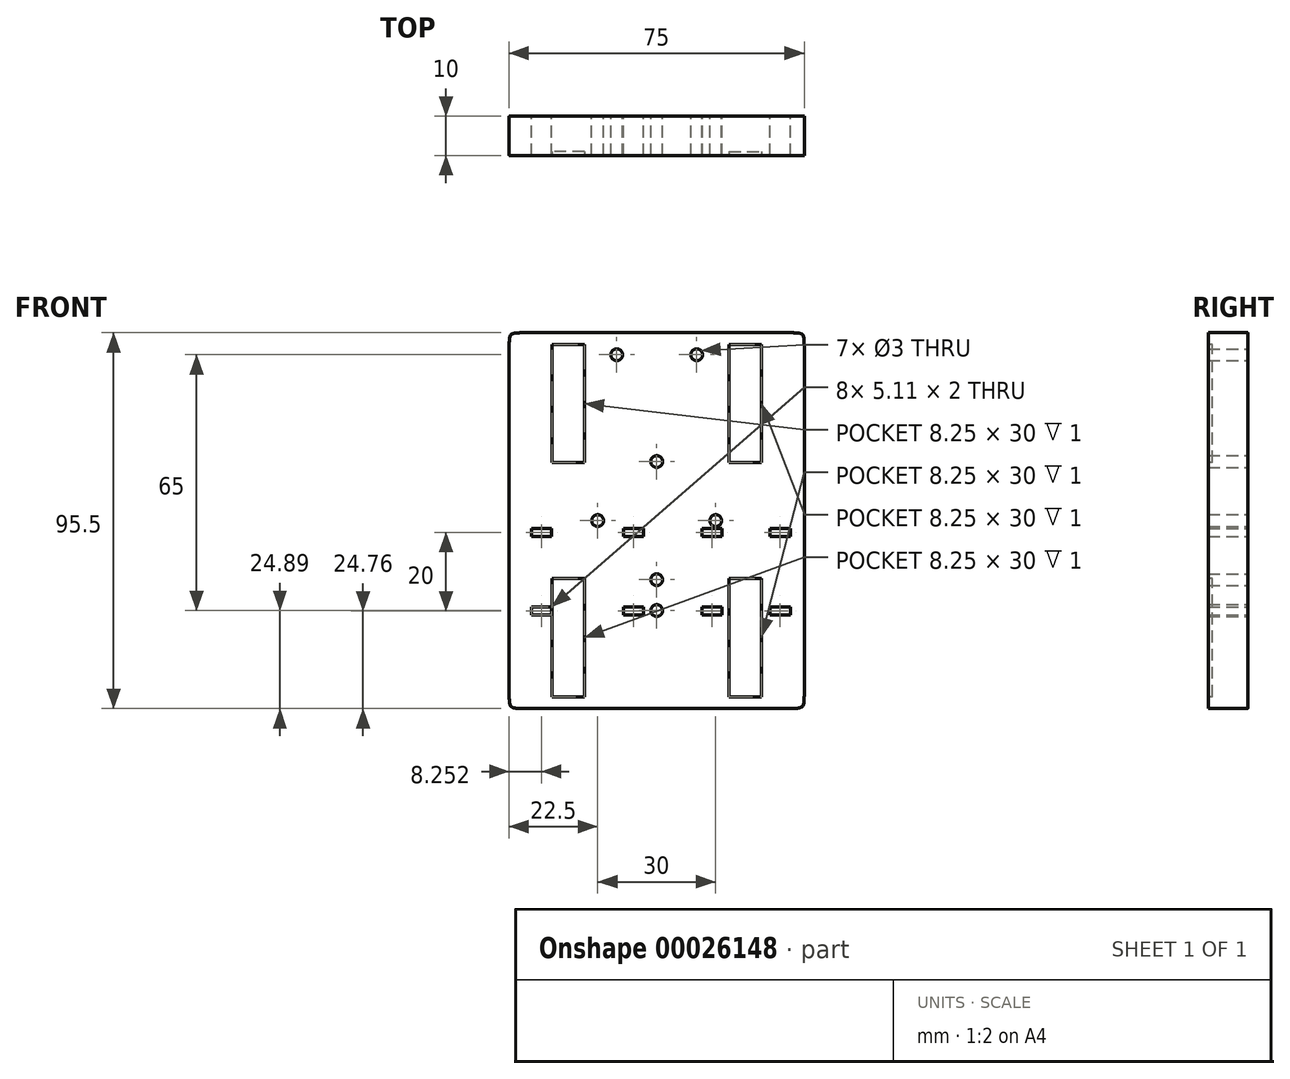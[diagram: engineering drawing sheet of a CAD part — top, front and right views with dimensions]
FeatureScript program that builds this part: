
annotation { "Feature Type Name" : "Feature", "Feature Type Description" : "" }
export const myFeature = defineFeature(function(context is Context, id is Id, definition is map)
    precondition{}
    {
        {
            var Q0;
            Q0=qCreatedBy(makeId("Front.planeOp"),FACE);
            var sketch = newSketch(context, id + "F0", { "sketchPlane" : qUnion([Q0])});
            skLineSegment(sketch, "E0.rect.bottom", {"start": v(37.5, -47.75) * mm, "end": v(-37.5, -47.75) * mm});
            skLineSegment(sketch, "E0.rect.top", {"start": v(37.5, 47.75) * mm, "end": v(-37.5, 47.75) * mm});
            skLineSegment(sketch, "E0.rect.left", {"start": v(37.5, -47.75) * mm, "end": v(37.5, 47.75) * mm});
            skLineSegment(sketch, "E0.rect.right", {"start": v(-37.5, -47.75) * mm, "end": v(-37.5, 47.75) * mm});
            skPoint(sketch, "E0.rect.middle", {"position": v(0, 0) * mm});
            skLineSegment(sketch, "E1.trimOffspring", {"start": v(-10.16, -22.86) * mm, "end": v(10.16, -22.86) * mm, "construction": true});
            skPoint(sketch, "E2", {"position": v(0, -22.86) * mm});
            skLineSegment(sketch, "E3", {"start": v(0, 47.75) * mm, "end": v(0, -47.75) * mm, "construction": true});
            skLineSegment(sketch, "E4", {"start": v(-22.5, 47.75) * mm, "end": v(-22.5, -47.75) * mm, "construction": true});
            skLineSegment(sketch, "E5", {"start": v(22.5, 47.75) * mm, "end": v(22.5, -47.75) * mm, "construction": true});
            skLineSegment(sketch, "E6", {"start": v(-22.5, 47.75) * mm, "end": v(22.5, -47.75) * mm, "construction": true});
            skLineSegment(sketch, "E7.rect.bottom", {"start": v(-18.37, 14.75) * mm, "end": v(-26.62, 14.75) * mm});
            skLineSegment(sketch, "E7.rect.top", {"start": v(-18.38, 44.75) * mm, "end": v(-26.63, 44.75) * mm});
            skLineSegment(sketch, "E7.rect.left", {"start": v(-18.37, 14.75) * mm, "end": v(-18.38, 44.75) * mm});
            skLineSegment(sketch, "E7.rect.right", {"start": v(-26.62, 14.75) * mm, "end": v(-26.63, 44.75) * mm});
            skPoint(sketch, "E7.rect.middle", {"position": v(-22.5, 29.75) * mm});
            skLineSegment(sketch, "E8.rect.bottom", {"start": v(-18.37, -44.75) * mm, "end": v(-26.62, -44.75) * mm});
            skLineSegment(sketch, "E8.rect.top", {"start": v(-18.37, -14.75) * mm, "end": v(-26.62, -14.75) * mm});
            skLineSegment(sketch, "E8.rect.left", {"start": v(-18.37, -44.75) * mm, "end": v(-18.37, -14.75) * mm});
            skLineSegment(sketch, "E8.rect.right", {"start": v(-26.62, -44.75) * mm, "end": v(-26.62, -14.75) * mm});
            skPoint(sketch, "E8.rect.middle", {"position": v(-22.5, -29.75) * mm});
            skLineSegment(sketch, "E9.rect.bottom", {"start": v(26.63, 14.75) * mm, "end": v(18.38, 14.75) * mm});
            skLineSegment(sketch, "E9.rect.top", {"start": v(26.62, 44.75) * mm, "end": v(18.37, 44.75) * mm});
            skLineSegment(sketch, "E9.rect.left", {"start": v(26.63, 14.75) * mm, "end": v(26.62, 44.75) * mm});
            skLineSegment(sketch, "E9.rect.right", {"start": v(18.38, 14.75) * mm, "end": v(18.37, 44.75) * mm});
            skPoint(sketch, "E9.rect.middle", {"position": v(22.5, 29.75) * mm});
            skLineSegment(sketch, "E10.rect.bottom", {"start": v(26.62, -14.75) * mm, "end": v(18.37, -14.75) * mm});
            skLineSegment(sketch, "E10.rect.top", {"start": v(26.62, -44.75) * mm, "end": v(18.38, -44.75) * mm});
            skLineSegment(sketch, "E10.rect.left", {"start": v(26.62, -14.75) * mm, "end": v(26.62, -44.75) * mm});
            skLineSegment(sketch, "E10.rect.right", {"start": v(18.37, -14.75) * mm, "end": v(18.38, -44.75) * mm});
            skPoint(sketch, "E10.rect.middle", {"position": v(22.5, -29.75) * mm});
            skLineSegment(sketch, "E11", {"start": v(-37.5, 44.75) * mm, "end": v(37.5, 44.75) * mm, "construction": true});
            skLineSegment(sketch, "E12", {"start": v(-37.5, -44.75) * mm, "end": v(37.5, -44.75) * mm, "construction": true});
            skPoint(sketch, "E13.orphan", {"position": v(37.5, 34.75) * mm});
            skPoint(sketch, "E14.orphan", {"position": v(0, 34.75) * mm});
            skPoint(sketch, "E15.start.orphan", {"position": v(-37.5, 34.75) * mm});
            skLineSegment(sketch, "E16", {"start": v(0, 0) * mm, "end": v(32.27, 0) * mm, "construction": true});
            skCircle(sketch, "E17.MirrorC", {"center": v(10.16, 42.14) * mm, "radius": 1.5 * mm});
            skCircle(sketch, "E18.MirrorC", {"center": v(-10.16, 42.14) * mm, "radius": 1.5 * mm});
            skCircle(sketch, "E19", {"center": v(0, 15) * mm, "radius": 1.5 * mm});
            skCircle(sketch, "E20.1.1", {"center": v(-15, 0) * mm, "radius": 1.5 * mm});
            skCircle(sketch, "E20.2.1", {"center": v(0, -15) * mm, "radius": 1.5 * mm});
            skCircle(sketch, "E20.3.1", {"center": v(15, 0) * mm, "radius": 1.5 * mm});
            skLineSegment(sketch, "E21", {"start": v(10.16, 42.14) * mm, "end": v(-10.16, 42.14) * mm, "construction": true});
            skLineSegment(sketch, "E22", {"start": v(-37.5, -2.99) * mm, "end": v(37.5, -2.99) * mm, "construction": true});
            skCircle(sketch, "E23", {"center": v(0, -22.86) * mm, "radius": 1.5 * mm});
            skLineSegment(sketch, "E24", {"start": v(-37.5, -22.99) * mm, "end": v(37.5, -22.99) * mm, "construction": true});
            skLineSegment(sketch, "E25.rect.bottom", {"start": v(-26.7, -3.99) * mm, "end": v(-31.8, -3.99) * mm});
            skLineSegment(sketch, "E25.rect.top", {"start": v(-26.7, -1.99) * mm, "end": v(-31.8, -1.99) * mm});
            skLineSegment(sketch, "E25.rect.left", {"start": v(-26.7, -3.99) * mm, "end": v(-26.7, -1.99) * mm});
            skLineSegment(sketch, "E25.rect.right", {"start": v(-31.8, -3.99) * mm, "end": v(-31.8, -1.99) * mm});
            skPoint(sketch, "E25.rect.middle", {"position": v(-29.25, -2.99) * mm});
            skLineSegment(sketch, "E26.rect.bottom", {"start": v(-8.4, -1.99) * mm, "end": v(-3.3, -1.99) * mm});
            skLineSegment(sketch, "E26.rect.top", {"start": v(-8.4, -4) * mm, "end": v(-3.3, -4) * mm});
            skLineSegment(sketch, "E26.rect.left", {"start": v(-8.4, -1.99) * mm, "end": v(-8.4, -4) * mm});
            skLineSegment(sketch, "E26.rect.right", {"start": v(-3.3, -1.99) * mm, "end": v(-3.3, -4) * mm});
            skPoint(sketch, "E26.rect.middle", {"position": v(-5.85, -2.99) * mm});
            skLineSegment(sketch, "E27.rect.bottom", {"start": v(-31.8, -21.99) * mm, "end": v(-26.7, -21.99) * mm});
            skLineSegment(sketch, "E27.rect.top", {"start": v(-31.8, -23.99) * mm, "end": v(-26.7, -23.99) * mm});
            skLineSegment(sketch, "E27.rect.left", {"start": v(-31.8, -21.99) * mm, "end": v(-31.8, -23.99) * mm});
            skLineSegment(sketch, "E27.rect.right", {"start": v(-26.7, -21.99) * mm, "end": v(-26.7, -23.99) * mm});
            skPoint(sketch, "E27.rect.middle", {"position": v(-29.25, -22.99) * mm});
            skLineSegment(sketch, "E28.rect.bottom", {"start": v(-8.4, -23.99) * mm, "end": v(-3.3, -23.99) * mm});
            skLineSegment(sketch, "E28.rect.top", {"start": v(-8.4, -21.99) * mm, "end": v(-3.3, -21.99) * mm});
            skLineSegment(sketch, "E28.rect.left", {"start": v(-8.4, -23.99) * mm, "end": v(-8.4, -21.99) * mm});
            skLineSegment(sketch, "E28.rect.right", {"start": v(-3.3, -23.99) * mm, "end": v(-3.3, -21.99) * mm});
            skPoint(sketch, "E28.rect.middle", {"position": v(-5.85, -22.99) * mm});
            skLineSegment(sketch, "E29.rect.bottom", {"start": v(11.48, -4) * mm, "end": v(16.6, -4) * mm});
            skLineSegment(sketch, "E29.rect.top", {"start": v(11.48, -1.99) * mm, "end": v(16.6, -1.99) * mm});
            skLineSegment(sketch, "E29.rect.left", {"start": v(11.48, -4) * mm, "end": v(11.48, -1.99) * mm});
            skLineSegment(sketch, "E29.rect.right", {"start": v(16.6, -4) * mm, "end": v(16.6, -1.99) * mm});
            skPoint(sketch, "E29.rect.middle", {"position": v(14.04, -2.99) * mm});
            skLineSegment(sketch, "E30.rect.bottom", {"start": v(11.48, -23.99) * mm, "end": v(16.6, -23.99) * mm});
            skLineSegment(sketch, "E30.rect.top", {"start": v(11.48, -22) * mm, "end": v(16.6, -22) * mm});
            skLineSegment(sketch, "E30.rect.left", {"start": v(11.48, -23.99) * mm, "end": v(11.48, -22) * mm});
            skLineSegment(sketch, "E30.rect.right", {"start": v(16.6, -23.99) * mm, "end": v(16.6, -22) * mm});
            skPoint(sketch, "E30.rect.middle", {"position": v(14.04, -22.99) * mm});
            skLineSegment(sketch, "E31.rect.bottom", {"start": v(28.82, -4) * mm, "end": v(33.93, -4) * mm});
            skLineSegment(sketch, "E31.rect.top", {"start": v(28.82, -1.99) * mm, "end": v(33.93, -1.99) * mm});
            skLineSegment(sketch, "E31.rect.left", {"start": v(28.82, -4) * mm, "end": v(28.82, -1.99) * mm});
            skLineSegment(sketch, "E31.rect.right", {"start": v(33.93, -4) * mm, "end": v(33.93, -1.99) * mm});
            skPoint(sketch, "E31.rect.middle", {"position": v(31.37, -2.99) * mm});
            skLineSegment(sketch, "E32.rect.bottom", {"start": v(33.93, -23.99) * mm, "end": v(28.82, -23.99) * mm});
            skLineSegment(sketch, "E32.rect.top", {"start": v(33.93, -21.99) * mm, "end": v(28.82, -21.99) * mm});
            skLineSegment(sketch, "E32.rect.left", {"start": v(33.93, -23.99) * mm, "end": v(33.93, -21.99) * mm});
            skLineSegment(sketch, "E32.rect.right", {"start": v(28.82, -23.99) * mm, "end": v(28.82, -21.99) * mm});
            skPoint(sketch, "E32.rect.middle", {"position": v(31.37, -22.99) * mm});
            skSolve(sketch);
        }
        {
            var Q0;
            Q0=makeQuery(id+"F0.imprint","IMPRINT",FACE,{"disambiguationData":[TD([[makeQuery(id+"F0.imprint","IMPRINT",EDGE,{"derivedFrom":sQuery(id+"F0.wireOp",EDGE,"E0.rect.bottom")}),-1.0]])]});
            var Q1;
            Q1=makeQuery(id+"F0.imprint","IMPRINT",FACE,{"disambiguationData":[TD([[makeQuery(id+"F0.imprint","IMPRINT",EDGE,{"derivedFrom":sQuery(id+"F0.wireOp",EDGE,"E7.rect.bottom")}),-1.0]])]});
            var Q2;
            Q2=makeQuery(id+"F0.imprint","IMPRINT",FACE,{"disambiguationData":[TD([[makeQuery(id+"F0.imprint","IMPRINT",EDGE,{"derivedFrom":sQuery(id+"F0.wireOp",EDGE,"E9.rect.bottom")}),-1.0]])]});
            var Q3;
            Q3=makeQuery(id+"F0.imprint","IMPRINT",FACE,{"disambiguationData":[TD([[makeQuery(id+"F0.imprint","IMPRINT",EDGE,{"derivedFrom":sQuery(id+"F0.wireOp",EDGE,"E8.rect.bottom")}),-1.0]])]});
            var Q4;
            Q4=makeQuery(id+"F0.imprint","IMPRINT",FACE,{"disambiguationData":[TD([[makeQuery(id+"F0.imprint","IMPRINT",EDGE,{"derivedFrom":sQuery(id+"F0.wireOp",EDGE,"E10.rect.bottom")}),1.0]])]});
            extrude(context, id + "F1", {"entities" : qUnion([Q0, Q1, Q2, Q3, Q4]), "depth" : 10 * mm});
        }
        {
            var Q0;
            Q0=makeQuery(id+"F1.opExtrude","CAP_FACE",FACE,{"disambiguationData":[OSD([sQuery(id+"F0.wireOp",EDGE,"E0.rect.bottom"),sQuery(id+"F0.wireOp",EDGE,"E0.rect.top"),sQuery(id+"F0.wireOp",EDGE,"E0.rect.left"),sQuery(id+"F0.wireOp",EDGE,"E0.rect.right"),sQuery(id+"F0.wireOp",EDGE,"1189089a-4ba9-4c00-a081-14e74841a8ab"),sQuery(id+"F0.wireOp",EDGE,"ac3c8be2-39e8-4b0b-97ec-68458567d3d3"),sQuery(id+"F0.wireOp",EDGE,"c879ed59-b1f7-4e12-a11a-ceb9f9b4f5f2")])],"isStart":false});
            var sketch = newSketch(context, id + "F2", { "sketchPlane" : qUnion([Q0])});
            skLineSegment(sketch, "E33", {"start": v(-37.5, 44.75) * mm, "end": v(37.5, 44.75) * mm, "construction": true});
            skLineSegment(sketch, "E34", {"start": v(37.5, -44.75) * mm, "end": v(-37.5, -44.75) * mm, "construction": true});
            skLineSegment(sketch, "E35", {"start": v(-22.5, 47.75) * mm, "end": v(-22.5, -47.75) * mm, "construction": true});
            skLineSegment(sketch, "E36", {"start": v(22.5, 47.75) * mm, "end": v(22.5, -47.75) * mm, "construction": true});
            skLineSegment(sketch, "E37", {"start": v(22.5, -47.75) * mm, "end": v(-22.5, 47.75) * mm, "construction": true});
            skPoint(sketch, "E38", {"position": v(0, 0) * mm});
            skLineSegment(sketch, "E39.rect.bottom", {"start": v(-18.37, 14.75) * mm, "end": v(-26.62, 14.75) * mm});
            skLineSegment(sketch, "E39.rect.top", {"start": v(-18.38, 44.75) * mm, "end": v(-26.63, 44.75) * mm});
            skLineSegment(sketch, "E39.rect.left", {"start": v(-18.37, 14.75) * mm, "end": v(-18.38, 44.75) * mm});
            skLineSegment(sketch, "E39.rect.right", {"start": v(-26.62, 14.75) * mm, "end": v(-26.63, 44.75) * mm});
            skPoint(sketch, "E39.rect.middle", {"position": v(-22.5, 29.75) * mm});
            skLineSegment(sketch, "E40.rect.bottom", {"start": v(18.38, 14.75) * mm, "end": v(26.63, 14.75) * mm});
            skLineSegment(sketch, "E40.rect.top", {"start": v(18.38, 44.75) * mm, "end": v(26.62, 44.75) * mm});
            skLineSegment(sketch, "E40.rect.left", {"start": v(18.38, 14.75) * mm, "end": v(18.38, 44.75) * mm});
            skLineSegment(sketch, "E40.rect.right", {"start": v(26.63, 14.75) * mm, "end": v(26.62, 44.75) * mm});
            skPoint(sketch, "E40.rect.middle", {"position": v(22.5, 29.75) * mm});
            skLineSegment(sketch, "E41.rect.bottom", {"start": v(-18.37, -44.75) * mm, "end": v(-26.62, -44.75) * mm});
            skLineSegment(sketch, "E41.rect.top", {"start": v(-18.37, -14.75) * mm, "end": v(-26.62, -14.75) * mm});
            skLineSegment(sketch, "E41.rect.left", {"start": v(-18.37, -44.75) * mm, "end": v(-18.37, -14.75) * mm});
            skLineSegment(sketch, "E41.rect.right", {"start": v(-26.62, -44.75) * mm, "end": v(-26.62, -14.75) * mm});
            skPoint(sketch, "E41.rect.middle", {"position": v(-22.5, -29.75) * mm});
            skLineSegment(sketch, "E42.rect.bottom", {"start": v(18.38, -44.75) * mm, "end": v(26.63, -44.75) * mm});
            skLineSegment(sketch, "E42.rect.top", {"start": v(18.38, -14.75) * mm, "end": v(26.62, -14.75) * mm});
            skLineSegment(sketch, "E42.rect.left", {"start": v(18.38, -44.75) * mm, "end": v(18.38, -14.75) * mm});
            skLineSegment(sketch, "E42.rect.right", {"start": v(26.63, -44.75) * mm, "end": v(26.62, -14.75) * mm});
            skPoint(sketch, "E42.rect.middle", {"position": v(22.5, -29.75) * mm});
            skSolve(sketch);
        }
        {
            var Q0;
            Q0=makeQuery(id+"F2.imprint","IMPRINT",FACE,{"disambiguationData":[TD([[makeQuery(id+"F2.imprint","IMPRINT",EDGE,{"derivedFrom":sQuery(id+"F2.wireOp",EDGE,"E39.rect.bottom")}),-1.0]])]});
            var Q1;
            Q1=makeQuery(id+"F2.imprint","IMPRINT",FACE,{"disambiguationData":[TD([[makeQuery(id+"F2.imprint","IMPRINT",EDGE,{"derivedFrom":sQuery(id+"F2.wireOp",EDGE,"E41.rect.bottom")}),-1.0]])]});
            var Q2;
            Q2=makeQuery(id+"F2.imprint","IMPRINT",FACE,{"disambiguationData":[TD([[makeQuery(id+"F2.imprint","IMPRINT",EDGE,{"derivedFrom":sQuery(id+"F2.wireOp",EDGE,"E40.rect.bottom")}),1.0]])]});
            var Q3;
            Q3=makeQuery(id+"F2.imprint","IMPRINT",FACE,{"disambiguationData":[TD([[makeQuery(id+"F2.imprint","IMPRINT",EDGE,{"derivedFrom":sQuery(id+"F2.wireOp",EDGE,"E42.rect.bottom")}),1.0]])]});
            extrude(context, id + "F3", {"entities" : qUnion([Q0, Q1, Q2, Q3]), "operationType" : NewBodyOperationType.REMOVE, "oppositeDirection" : true, "depth" : 1 * mm});
        }
        {
            var Q0;
            Q0=makeQuery(id+"F1.opExtrude","SWEPT_EDGE",EDGE,{"disambiguationData":[OSD([sQuery(id+"F0.wireOp",EDGE,"E0.rect.top"),sQuery(id+"F0.wireOp",EDGE,"E0.rect.left")])]});
            var Q1;
            Q1=makeQuery(id+"F1.opExtrude","SWEPT_EDGE",EDGE,{"disambiguationData":[OSD([sQuery(id+"F0.wireOp",EDGE,"E0.rect.bottom"),sQuery(id+"F0.wireOp",EDGE,"E0.rect.left")])]});
            var Q2;
            Q2=makeQuery(id+"F1.opExtrude","SWEPT_EDGE",EDGE,{"disambiguationData":[OSD([sQuery(id+"F0.wireOp",EDGE,"E0.rect.bottom"),sQuery(id+"F0.wireOp",EDGE,"E0.rect.right")])]});
            var Q3;
            Q3=makeQuery(id+"F1.opExtrude","SWEPT_EDGE",EDGE,{"disambiguationData":[OSD([sQuery(id+"F0.wireOp",EDGE,"E0.rect.top"),sQuery(id+"F0.wireOp",EDGE,"E0.rect.right")])]});
            fillet(context, id + "F4", {"entities" : qUnion([Q0, Q1, Q2, Q3]), "radius" : 5 * mm, "rho" : 0.8, "crossSection" : FilletCrossSection.CONIC, "allowEdgeOverflow" : false});
        }
    });
